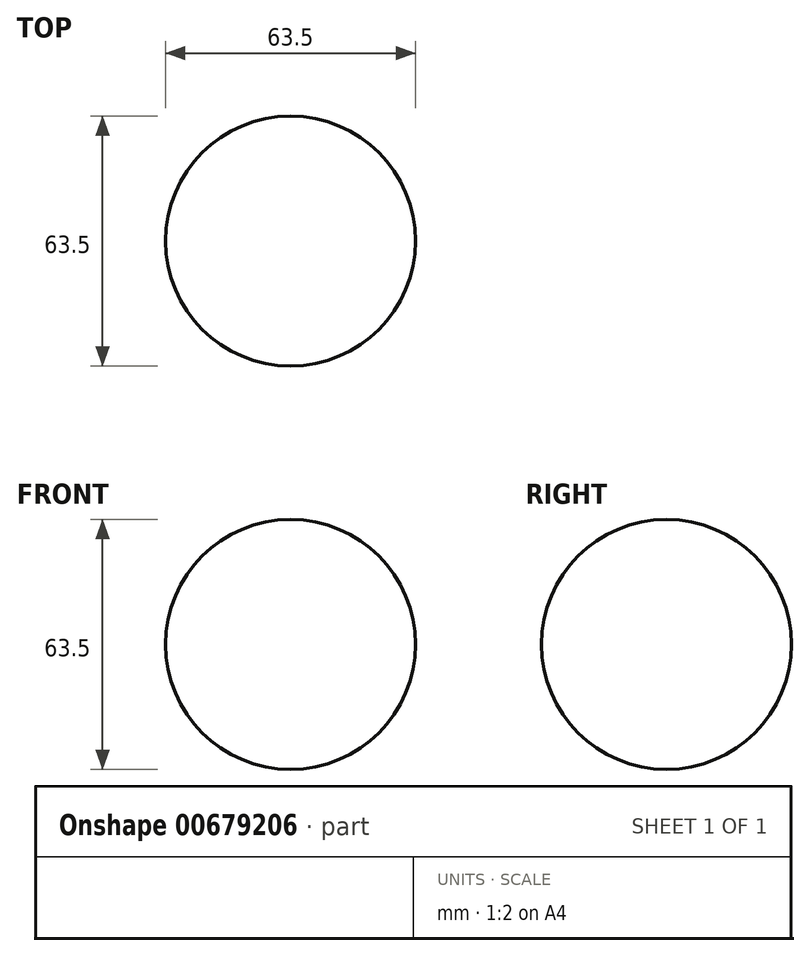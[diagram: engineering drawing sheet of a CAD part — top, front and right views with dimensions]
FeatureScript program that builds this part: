
annotation { "Feature Type Name" : "Feature", "Feature Type Description" : "" }
export const myFeature = defineFeature(function(context is Context, id is Id, definition is map)
    precondition{}
    {
        {
            var Q0;
            Q0=qCreatedBy(makeId("Top.planeOp"),FACE);
            var sketch = newSketch(context, id + "F0", { "sketchPlane" : qUnion([Q0])});
            skArc(sketch, "E0", {"start": v(0, 31.75) * mm, "mid": v(-31.75, 0) * mm, "end": v(0, -31.75) * mm});
            skLineSegment(sketch, "E1", {"start": v(0, 0) * mm, "end": v(0, 31.75) * mm});
            skLineSegment(sketch, "E2", {"start": v(0, 31.75) * mm, "end": v(0, -31.75) * mm});
            skSolve(sketch);
        }
        {
            var Q0;
            {var subQ0=sQuery(id+"F0.wireOp",EDGE,"E0");Q0=makeQuery(id+"F0.imprint","IMPRINT",FACE,{"disambiguationData":[TD([[makeQuery(id+"F0.imprint","IMPRINT",EDGE,{"derivedFrom":subQ0}),1.0]])]});}
            var Q1;
            Q1=sQuery(id+"F0.wireOp",EDGE,"E2");
            revolve(context, id + "F1", {"entities" : qUnion([Q0]), "axis" : qUnion([Q1]), "revolveType" : RevolveType.FULL});
        }
    });
